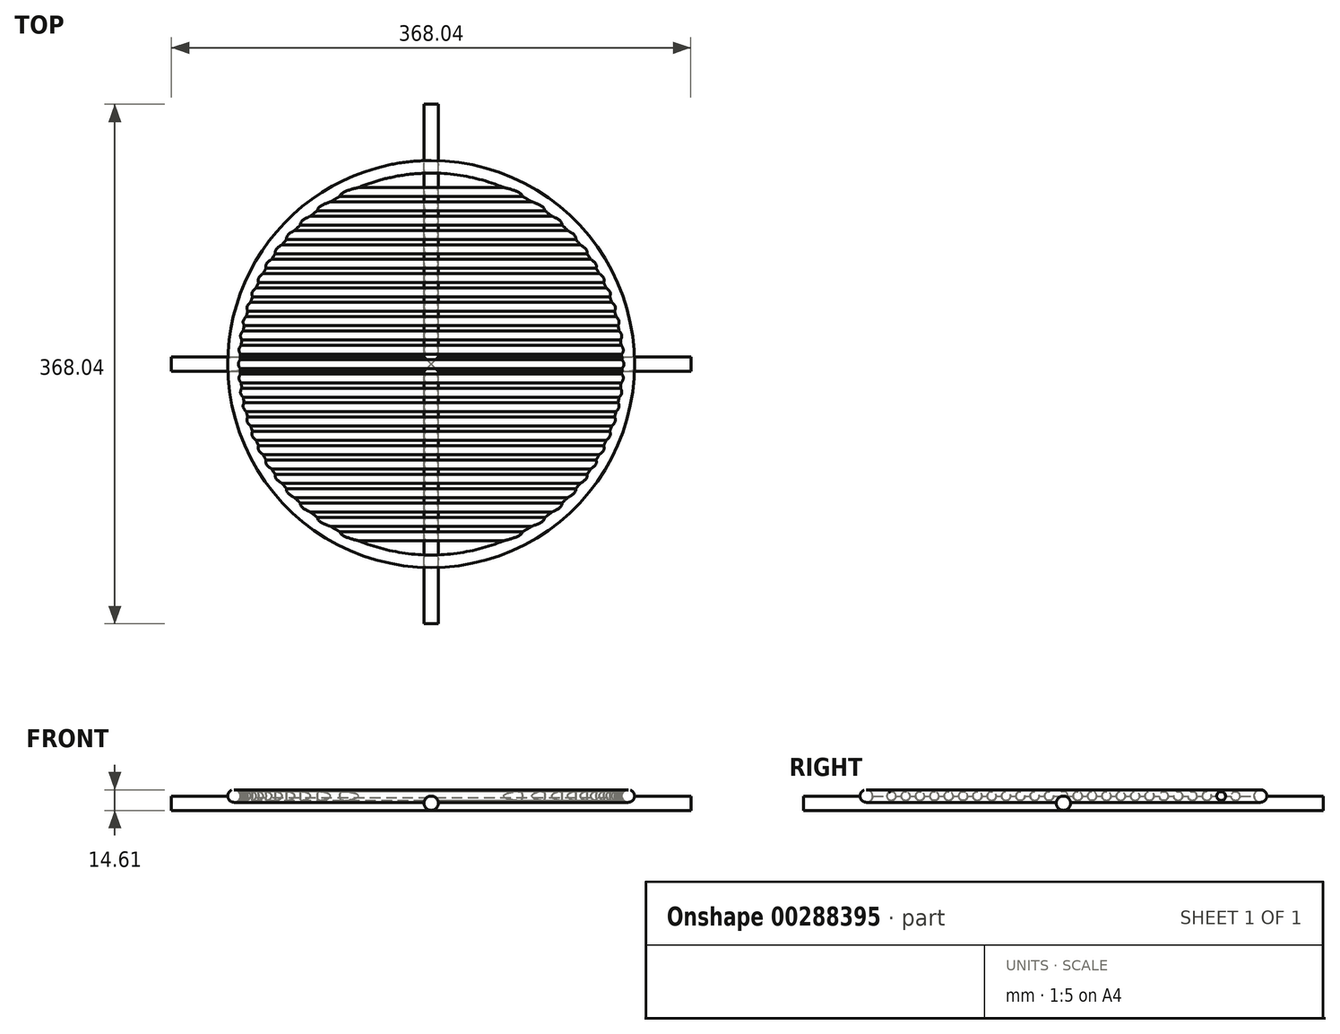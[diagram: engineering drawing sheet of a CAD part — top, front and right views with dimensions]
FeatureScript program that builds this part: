
annotation { "Feature Type Name" : "Feature", "Feature Type Description" : "" }
export const myFeature = defineFeature(function(context is Context, id is Id, definition is map)
    precondition{}
    {
        {
            var Q0;
            Q0=qCreatedBy(makeId("Top.planeOp"),FACE);
            var sketch = newSketch(context, id + "F0", { "sketchPlane" : qUnion([Q0])});
            skCircle(sketch, "E0.0.0", {"center": v(0, 0) * mm, "radius": 158.75 * mm, "construction": true});
            skCircle(sketch, "E1.0", {"center": v(0, 0) * mm, "radius": 139.7 * mm, "construction": true});
            skLineSegment(sketch, "E2", {"start": v(-158.62, 0) * mm, "end": v(158.62, 0) * mm});
            skLineSegment(sketch, "E3", {"start": v(0, 158.62) * mm, "end": v(0, -158.62) * mm});
            skLineSegment(sketch, "E4.bottom", {"start": v(-6.35, 158.62) * mm, "end": v(6.35, 158.62) * mm, "construction": true});
            skLineSegment(sketch, "E4.top", {"start": v(-6.35, 139.56) * mm, "end": v(6.35, 139.56) * mm, "construction": true});
            skLineSegment(sketch, "E4.left", {"start": v(-6.35, 158.62) * mm, "end": v(-6.35, 139.56) * mm, "construction": true});
            skLineSegment(sketch, "E4.right", {"start": v(6.35, 158.62) * mm, "end": v(6.35, 139.56) * mm, "construction": true});
            skLineSegment(sketch, "E5.bottom", {"start": v(-158.62, -6.35) * mm, "end": v(-139.56, -6.35) * mm, "construction": true});
            skLineSegment(sketch, "E5.top", {"start": v(-158.62, 6.35) * mm, "end": v(-139.56, 6.35) * mm, "construction": true});
            skLineSegment(sketch, "E5.left", {"start": v(-158.62, -6.35) * mm, "end": v(-158.62, 6.35) * mm, "construction": true});
            skLineSegment(sketch, "E5.right", {"start": v(-139.56, -6.35) * mm, "end": v(-139.56, 6.35) * mm, "construction": true});
            skLineSegment(sketch, "E6.bottom", {"start": v(158.62, 6.35) * mm, "end": v(139.56, 6.35) * mm, "construction": true});
            skLineSegment(sketch, "E6.top", {"start": v(158.62, -6.35) * mm, "end": v(139.56, -6.35) * mm, "construction": true});
            skLineSegment(sketch, "E6.left", {"start": v(158.62, 6.35) * mm, "end": v(158.62, -6.35) * mm, "construction": true});
            skLineSegment(sketch, "E6.right", {"start": v(139.56, 6.35) * mm, "end": v(139.56, -6.35) * mm, "construction": true});
            skLineSegment(sketch, "E7.bottom", {"start": v(6.35, -158.62) * mm, "end": v(-6.35, -158.62) * mm, "construction": true});
            skLineSegment(sketch, "E7.top", {"start": v(6.35, -139.56) * mm, "end": v(-6.35, -139.56) * mm, "construction": true});
            skLineSegment(sketch, "E7.left", {"start": v(6.35, -158.62) * mm, "end": v(6.35, -139.56) * mm, "construction": true});
            skLineSegment(sketch, "E7.right", {"start": v(-6.35, -158.62) * mm, "end": v(-6.35, -139.56) * mm, "construction": true});
            skPoint(sketch, "E8", {"position": v(158.62, 0) * mm});
            skPoint(sketch, "E9", {"position": v(0, -158.62) * mm});
            skPoint(sketch, "E10", {"position": v(0, 158.62) * mm});
            skPoint(sketch, "E11", {"position": v(-158.62, 0) * mm});
            skSolve(sketch);
        }
        {
            var Q0;
            Q0=sQuery(id+"F0.wireOp",VERTEX,"E11");
            var Q1;
            Q1=qCreatedBy(makeId("Right.planeOp"),FACE);
            cPlane(context, id + "F1", {"entities" : qUnion([Q0, Q1]), "cplaneType" : CPlaneType.PLANE_POINT, "offset" : 25.4 * mm, "width" : 152.4 * mm, "height" : 152.4 * mm});
        }
        {
            var Q0;
            Q0=qCreatedBy(id+"F1.planeOp",FACE);
            var sketch = newSketch(context, id + "F2", { "sketchPlane" : qUnion([Q0])});
            skPoint(sketch, "E12.0", {"position": v(0, 0) * mm});
            skCircle(sketch, "E13", {"center": v(0, 0) * mm, "radius": 5.08 * mm});
            skPoint(sketch, "E14", {"position": v(0, 5.08) * mm});
            skSolve(sketch);
        }
        {
            var Q0;
            Q0=sQuery(id+"F0.wireOp",VERTEX,"E9");
            var Q1;
            Q1=qCreatedBy(makeId("Front.planeOp"),FACE);
            cPlane(context, id + "F3", {"entities" : qUnion([Q0, Q1]), "cplaneType" : CPlaneType.PLANE_POINT, "offset" : 25.4 * mm, "width" : 152.4 * mm, "height" : 152.4 * mm});
        }
        {
            var Q0;
            Q0=qCreatedBy(id+"F3.planeOp",FACE);
            var sketch = newSketch(context, id + "F4", { "sketchPlane" : qUnion([Q0])});
            skCircle(sketch, "E15", {"center": v(0, 0) * mm, "radius": 5.08 * mm});
            skSolve(sketch);
        }
        {
            var Q0;
            Q0=sQuery(id+"F2.wireOp",VERTEX,"E14");
            var Q1;
            Q1=qCreatedBy(makeId("Top.planeOp"),FACE);
            cPlane(context, id + "F5", {"entities" : qUnion([Q0, Q1]), "cplaneType" : CPlaneType.PLANE_POINT, "offset" : 25.4 * mm, "width" : 152.4 * mm, "height" : 152.4 * mm});
        }
        {
            var Q0;
            Q0=qCreatedBy(id+"F5.planeOp",FACE);
            var sketch = newSketch(context, id + "F6", { "sketchPlane" : qUnion([Q0])});
            skCircle(sketch, "E16.0", {"center": v(0, 0) * mm, "radius": 139.7 * mm});
            skLineSegment(sketch, "E17", {"start": v(-139.7, 0) * mm, "end": v(139.7, 0) * mm});
            skLineSegment(sketch, "E18", {"start": v(-139.33, -10.16) * mm, "end": v(139.33, -10.16) * mm});
            skLineSegment(sketch, "E19", {"start": v(-138.21, -20.32) * mm, "end": v(138.21, -20.32) * mm});
            skLineSegment(sketch, "E20", {"start": v(136.33, -30.48) * mm, "end": v(-136.33, -30.48) * mm});
            skLineSegment(sketch, "E21", {"start": v(-133.66, -40.64) * mm, "end": v(133.66, -40.64) * mm});
            skLineSegment(sketch, "E22", {"start": v(130.14, -50.8) * mm, "end": v(-130.14, -50.8) * mm});
            skLineSegment(sketch, "E23", {"start": v(-125.7, -60.96) * mm, "end": v(125.7, -60.96) * mm});
            skLineSegment(sketch, "E24", {"start": v(120.24, -71.12) * mm, "end": v(-120.24, -71.12) * mm});
            skLineSegment(sketch, "E25", {"start": v(-113.62, -81.28) * mm, "end": v(113.62, -81.28) * mm});
            skLineSegment(sketch, "E26", {"start": v(-105.62, -91.44) * mm, "end": v(105.62, -91.44) * mm});
            skLineSegment(sketch, "E27", {"start": v(-95.88, -101.6) * mm, "end": v(95.88, -101.6) * mm});
            skLineSegment(sketch, "E28", {"start": v(-83.82, -111.76) * mm, "end": v(83.82, -111.76) * mm});
            skLineSegment(sketch, "E29", {"start": v(-68.2, -121.92) * mm, "end": v(68.2, -121.92) * mm});
            skLineSegment(sketch, "E30", {"start": v(0, 139.7) * mm, "end": v(0, -139.7) * mm, "construction": true});
            skLineSegment(sketch, "E31.MirrorCS", {"start": v(-139.33, 10.16) * mm, "end": v(139.33, 10.16) * mm});
            skLineSegment(sketch, "E32.MirrorCS", {"start": v(-138.21, 20.32) * mm, "end": v(138.21, 20.32) * mm});
            skLineSegment(sketch, "E33.MirrorCS", {"start": v(136.33, 30.48) * mm, "end": v(-136.33, 30.48) * mm});
            skLineSegment(sketch, "E34.MirrorCS", {"start": v(-133.66, 40.64) * mm, "end": v(133.66, 40.64) * mm});
            skLineSegment(sketch, "E35.MirrorCS", {"start": v(130.14, 50.8) * mm, "end": v(-130.14, 50.8) * mm});
            skLineSegment(sketch, "E36.MirrorCS", {"start": v(-125.7, 60.96) * mm, "end": v(125.7, 60.96) * mm});
            skLineSegment(sketch, "E37.MirrorCS", {"start": v(120.24, 71.12) * mm, "end": v(-120.24, 71.12) * mm});
            skLineSegment(sketch, "E38.MirrorCS", {"start": v(-113.62, 81.28) * mm, "end": v(113.62, 81.28) * mm});
            skLineSegment(sketch, "E39.MirrorCS", {"start": v(-105.62, 91.44) * mm, "end": v(105.62, 91.44) * mm});
            skLineSegment(sketch, "E40.MirrorCS", {"start": v(-95.88, 101.6) * mm, "end": v(95.88, 101.6) * mm});
            skLineSegment(sketch, "E41.MirrorCS", {"start": v(-83.82, 111.76) * mm, "end": v(83.82, 111.76) * mm});
            skLineSegment(sketch, "E42.MirrorCS", {"start": v(-68.2, 121.92) * mm, "end": v(68.2, 121.92) * mm});
            skSolve(sketch);
        }
        {
            var Q0;
            Q0=sQuery(id+"F6.wireOp",VERTEX,"E30.start");
            var Q1;
            Q1=qCreatedBy(makeId("Right.planeOp"),FACE);
            cPlane(context, id + "F7", {"entities" : qUnion([Q0, Q1]), "cplaneType" : CPlaneType.PLANE_POINT, "offset" : 25.4 * mm, "width" : 152.4 * mm, "height" : 152.4 * mm});
        }
        {
            var Q0;
            Q0=qCreatedBy(id+"F7.planeOp",FACE);
            var sketch = newSketch(context, id + "F8", { "sketchPlane" : qUnion([Q0])});
            skPoint(sketch, "E43.0", {"position": v(139.7, 5.08) * mm});
            skCircle(sketch, "E44", {"center": v(139.7, 5.08) * mm, "radius": 4.45 * mm});
            skSolve(sketch);
        }
        {
            var Q0;
            Q0=makeQuery(id+"F8.imprint","IMPRINT",FACE,{"disambiguationData":[TD([[makeQuery(id+"F8.imprint","IMPRINT",EDGE,{"derivedFrom":sQuery(id+"F8.wireOp",EDGE,"E44")}),1.0]])]});
            var Q1;
            Q1=sQuery(id+"F6.wireOp",EDGE,"E16.0");
            sweep(context, id + "F9", {"profiles" : qUnion([Q0]), "path" : qUnion([Q1])});
        }
        {
            var Q0;
            Q0=sQuery(id+"F6.wireOp",VERTEX,"E42.MirrorCS.end");
            var Q1;
            Q1=qCreatedBy(makeId("Right.planeOp"),FACE);
            cPlane(context, id + "F10", {"entities" : qUnion([Q0, Q1]), "cplaneType" : CPlaneType.PLANE_POINT, "offset" : 25.4 * mm, "width" : 152.4 * mm, "height" : 152.4 * mm});
        }
        {
            var Q0;
            Q0=qCreatedBy(id+"F10.planeOp",FACE);
            var sketch = newSketch(context, id + "F11", { "sketchPlane" : qUnion([Q0])});
            skPoint(sketch, "E45.0", {"position": v(121.92, 5.08) * mm});
            skCircle(sketch, "E46", {"center": v(121.92, 5.08) * mm, "radius": 3.18 * mm});
            skSolve(sketch);
        }
        {
            var Q0;
            Q0=sQuery(id+"F6.wireOp",VERTEX,"E41.MirrorCS.end");
            var Q1;
            Q1=qCreatedBy(id+"F10.planeOp",FACE);
            cPlane(context, id + "F12", {"entities" : qUnion([Q0, Q1]), "cplaneType" : CPlaneType.PLANE_POINT, "offset" : 25.4 * mm, "width" : 152.4 * mm, "height" : 152.4 * mm});
        }
        {
            var Q0;
            Q0=qCreatedBy(id+"F12.planeOp",FACE);
            var sketch = newSketch(context, id + "F13", { "sketchPlane" : qUnion([Q0])});
            skPoint(sketch, "E47.0", {"position": v(111.76, 5.08) * mm});
            skCircle(sketch, "E48", {"center": v(111.76, 5.08) * mm, "radius": 3.18 * mm});
            skSolve(sketch);
        }
        {
            var Q0;
            Q0=makeQuery(id+"F13.imprint","IMPRINT",FACE,{"disambiguationData":[TD([[makeQuery(id+"F13.imprint","IMPRINT",EDGE,{"derivedFrom":sQuery(id+"F13.wireOp",EDGE,"E48")}),1.0]])]});
            var Q1;
            Q1=sQuery(id+"F6.wireOp",EDGE,"E41.MirrorCS");
            sweep(context, id + "F14", {"profiles" : qUnion([Q0]), "path" : qUnion([Q1])});
        }
        {
            var Q0;
            Q0=makeQuery(id+"F11.imprint","IMPRINT",FACE,{"disambiguationData":[TD([[makeQuery(id+"F11.imprint","IMPRINT",EDGE,{"derivedFrom":sQuery(id+"F11.wireOp",EDGE,"E46")}),1.0]])]});
            var Q1;
            Q1=sQuery(id+"F6.wireOp",EDGE,"E42.MirrorCS");
            sweep(context, id + "F15", {"profiles" : qUnion([Q0]), "path" : qUnion([Q1])});
        }
        {
            var Q0;
            Q0=sQuery(id+"F6.wireOp",VERTEX,"E40.MirrorCS.end");
            var Q1;
            Q1=qCreatedBy(id+"F12.planeOp",FACE);
            cPlane(context, id + "F16", {"entities" : qUnion([Q0, Q1]), "cplaneType" : CPlaneType.PLANE_POINT, "offset" : 25.4 * mm, "width" : 152.4 * mm, "height" : 152.4 * mm});
        }
        {
            var Q0;
            Q0=qCreatedBy(id+"F16.planeOp",FACE);
            var sketch = newSketch(context, id + "F17", { "sketchPlane" : qUnion([Q0])});
            skPoint(sketch, "E49.0", {"position": v(101.6, 5.08) * mm});
            skCircle(sketch, "E50", {"center": v(101.6, 5.08) * mm, "radius": 3.18 * mm});
            skSolve(sketch);
        }
        {
            var Q0;
            Q0=makeQuery(id+"F17.imprint","IMPRINT",FACE,{"disambiguationData":[TD([[makeQuery(id+"F17.imprint","IMPRINT",EDGE,{"derivedFrom":sQuery(id+"F17.wireOp",EDGE,"E50")}),1.0]])]});
            var Q1;
            Q1=sQuery(id+"F6.wireOp",EDGE,"E40.MirrorCS");
            sweep(context, id + "F18", {"operationType" : NewBodyOperationType.ADD, "profiles" : qUnion([Q0]), "path" : qUnion([Q1])});
        }
        {
            var Q0;
            Q0=makeQuery(id+"F17.imprint","IMPRINT",FACE,{"disambiguationData":[TD([[makeQuery(id+"F17.imprint","IMPRINT",EDGE,{"derivedFrom":sQuery(id+"F17.wireOp",EDGE,"E50")}),1.0]])]});
            var Q1;
            Q1=sQuery(id+"F6.wireOp",EDGE,"E40.MirrorCS");
            sweep(context, id + "F19", {"profiles" : qUnion([Q0]), "path" : qUnion([Q1])});
        }
        {
            var Q0;
            Q0=sQuery(id+"F6.wireOp",VERTEX,"E39.MirrorCS.end");
            var Q1;
            Q1=qCreatedBy(id+"F16.planeOp",FACE);
            cPlane(context, id + "F20", {"entities" : qUnion([Q0, Q1]), "cplaneType" : CPlaneType.PLANE_POINT, "offset" : 25.4 * mm, "width" : 152.4 * mm, "height" : 152.4 * mm});
        }
        {
            var Q0;
            Q0=qCreatedBy(id+"F20.planeOp",FACE);
            var sketch = newSketch(context, id + "F21", { "sketchPlane" : qUnion([Q0])});
            skPoint(sketch, "E51.0", {"position": v(91.44, 5.08) * mm});
            skCircle(sketch, "E52", {"center": v(91.44, 5.08) * mm, "radius": 3.18 * mm});
            skSolve(sketch);
        }
        {
            var Q0;
            Q0=makeQuery(id+"F21.imprint","IMPRINT",FACE,{"disambiguationData":[TD([[makeQuery(id+"F21.imprint","IMPRINT",EDGE,{"derivedFrom":sQuery(id+"F21.wireOp",EDGE,"E52")}),1.0]])]});
            var Q1;
            Q1=sQuery(id+"F6.wireOp",EDGE,"E39.MirrorCS");
            sweep(context, id + "F22", {"profiles" : qUnion([Q0]), "path" : qUnion([Q1])});
        }
        {
            var Q0;
            Q0=sQuery(id+"F6.wireOp",VERTEX,"E38.MirrorCS.end");
            var Q1;
            Q1=qCreatedBy(id+"F16.planeOp",FACE);
            cPlane(context, id + "F23", {"entities" : qUnion([Q0, Q1]), "cplaneType" : CPlaneType.PLANE_POINT, "offset" : 25.4 * mm, "width" : 152.4 * mm, "height" : 152.4 * mm});
        }
        {
            var Q0;
            Q0=qCreatedBy(id+"F23.planeOp",FACE);
            var sketch = newSketch(context, id + "F24", { "sketchPlane" : qUnion([Q0])});
            skPoint(sketch, "E53.0", {"position": v(81.28, 5.08) * mm});
            skCircle(sketch, "E54", {"center": v(81.28, 5.08) * mm, "radius": 3.18 * mm});
            skSolve(sketch);
        }
        {
            var Q0;
            Q0=sQuery(id+"F6.wireOp",VERTEX,"E37.MirrorCS.start");
            var Q1;
            Q1=qCreatedBy(id+"F16.planeOp",FACE);
            cPlane(context, id + "F25", {"entities" : qUnion([Q0, Q1]), "cplaneType" : CPlaneType.PLANE_POINT, "offset" : 25.4 * mm, "width" : 152.4 * mm, "height" : 152.4 * mm});
        }
        {
            var Q0;
            Q0=qCreatedBy(id+"F25.planeOp",FACE);
            var sketch = newSketch(context, id + "F26", { "sketchPlane" : qUnion([Q0])});
            skPoint(sketch, "E55.0", {"position": v(71.12, 5.08) * mm});
            skCircle(sketch, "E56", {"center": v(71.12, 5.08) * mm, "radius": 3.18 * mm});
            skSolve(sketch);
        }
        {
            var Q0;
            Q0=sQuery(id+"F6.wireOp",VERTEX,"E36.MirrorCS.end");
            var Q1;
            Q1=qCreatedBy(id+"F16.planeOp",FACE);
            cPlane(context, id + "F27", {"entities" : qUnion([Q0, Q1]), "cplaneType" : CPlaneType.PLANE_POINT, "offset" : 25.4 * mm, "width" : 152.4 * mm, "height" : 152.4 * mm});
        }
        {
            var Q0;
            Q0=qCreatedBy(id+"F27.planeOp",FACE);
            var sketch = newSketch(context, id + "F28", { "sketchPlane" : qUnion([Q0])});
            skPoint(sketch, "E57.0", {"position": v(60.96, 5.08) * mm});
            skCircle(sketch, "E58", {"center": v(60.96, 5.08) * mm, "radius": 3.18 * mm});
            skSolve(sketch);
        }
        {
            var Q0;
            Q0=sQuery(id+"F6.wireOp",VERTEX,"E35.MirrorCS.start");
            var Q1;
            Q1=qCreatedBy(id+"F16.planeOp",FACE);
            cPlane(context, id + "F29", {"entities" : qUnion([Q0, Q1]), "cplaneType" : CPlaneType.PLANE_POINT, "offset" : 25.4 * mm, "width" : 152.4 * mm, "height" : 152.4 * mm});
        }
        {
            var Q0;
            Q0=qCreatedBy(id+"F29.planeOp",FACE);
            var sketch = newSketch(context, id + "F30", { "sketchPlane" : qUnion([Q0])});
            skPoint(sketch, "E59.0", {"position": v(50.8, 5.08) * mm});
            skCircle(sketch, "E60", {"center": v(50.8, 5.08) * mm, "radius": 3.18 * mm});
            skSolve(sketch);
        }
        {
            var Q0;
            Q0=sQuery(id+"F6.wireOp",VERTEX,"E34.MirrorCS.end");
            var Q1;
            Q1=qCreatedBy(id+"F16.planeOp",FACE);
            cPlane(context, id + "F31", {"entities" : qUnion([Q0, Q1]), "cplaneType" : CPlaneType.PLANE_POINT, "offset" : 25.4 * mm, "width" : 152.4 * mm, "height" : 152.4 * mm});
        }
        {
            var Q0;
            Q0=qCreatedBy(id+"F31.planeOp",FACE);
            var sketch = newSketch(context, id + "F32", { "sketchPlane" : qUnion([Q0])});
            skPoint(sketch, "E61.0", {"position": v(40.64, 5.08) * mm});
            skCircle(sketch, "E62", {"center": v(40.64, 5.08) * mm, "radius": 3.18 * mm});
            skSolve(sketch);
        }
        {
            var Q0;
            Q0=sQuery(id+"F6.wireOp",VERTEX,"E33.MirrorCS.start");
            var Q1;
            Q1=qCreatedBy(id+"F10.planeOp",FACE);
            cPlane(context, id + "F33", {"entities" : qUnion([Q0, Q1]), "cplaneType" : CPlaneType.PLANE_POINT, "offset" : 25.4 * mm, "width" : 152.4 * mm, "height" : 152.4 * mm});
        }
        {
            var Q0;
            Q0=qCreatedBy(id+"F33.planeOp",FACE);
            var sketch = newSketch(context, id + "F34", { "sketchPlane" : qUnion([Q0])});
            skPoint(sketch, "E63.0", {"position": v(30.48, 5.08) * mm});
            skCircle(sketch, "E64", {"center": v(30.48, 5.08) * mm, "radius": 3.17 * mm});
            skSolve(sketch);
        }
        {
            var Q0;
            Q0=sQuery(id+"F6.wireOp",VERTEX,"E32.MirrorCS.end");
            var Q1;
            Q1=qCreatedBy(id+"F12.planeOp",FACE);
            cPlane(context, id + "F35", {"entities" : qUnion([Q0, Q1]), "cplaneType" : CPlaneType.PLANE_POINT, "offset" : 25.4 * mm, "width" : 152.4 * mm, "height" : 152.4 * mm});
        }
        {
            var Q0;
            Q0=qCreatedBy(id+"F35.planeOp",FACE);
            var sketch = newSketch(context, id + "F36", { "sketchPlane" : qUnion([Q0])});
            skPoint(sketch, "E65.0", {"position": v(20.32, 5.08) * mm});
            skCircle(sketch, "E66", {"center": v(20.32, 5.08) * mm, "radius": 3.18 * mm});
            skSolve(sketch);
        }
        {
            var Q0;
            Q0=sQuery(id+"F6.wireOp",VERTEX,"E31.MirrorCS.end");
            var Q1;
            Q1=qCreatedBy(id+"F31.planeOp",FACE);
            cPlane(context, id + "F37", {"entities" : qUnion([Q0, Q1]), "cplaneType" : CPlaneType.PLANE_POINT, "offset" : 25.4 * mm, "width" : 152.4 * mm, "height" : 152.4 * mm});
        }
        {
            var Q0;
            Q0=qCreatedBy(id+"F37.planeOp",FACE);
            var sketch = newSketch(context, id + "F38", { "sketchPlane" : qUnion([Q0])});
            skPoint(sketch, "E67.0", {"position": v(10.16, 5.08) * mm});
            skCircle(sketch, "E68", {"center": v(10.16, 5.08) * mm, "radius": 3.18 * mm});
            skSolve(sketch);
        }
        {
            var Q0;
            Q0=sQuery(id+"F6.wireOp",VERTEX,"E17.end");
            var Q1;
            Q1=qCreatedBy(id+"F16.planeOp",FACE);
            cPlane(context, id + "F39", {"entities" : qUnion([Q0, Q1]), "cplaneType" : CPlaneType.PLANE_POINT, "offset" : 25.4 * mm, "width" : 152.4 * mm, "height" : 152.4 * mm});
        }
        {
            var Q0;
            Q0=qCreatedBy(id+"F39.planeOp",FACE);
            var sketch = newSketch(context, id + "F40", { "sketchPlane" : qUnion([Q0])});
            skPoint(sketch, "E69.0", {"position": v(0, 5.08) * mm});
            skCircle(sketch, "E70", {"center": v(0, 5.08) * mm, "radius": 3.18 * mm});
            skSolve(sketch);
        }
        {
            var Q0;
            Q0=makeQuery(id+"F24.imprint","IMPRINT",FACE,{"disambiguationData":[TD([[makeQuery(id+"F24.imprint","IMPRINT",EDGE,{"derivedFrom":sQuery(id+"F24.wireOp",EDGE,"E54")}),1.0]])]});
            var Q1;
            Q1=sQuery(id+"F6.wireOp",EDGE,"E38.MirrorCS");
            sweep(context, id + "F41", {"profiles" : qUnion([Q0]), "path" : qUnion([Q1])});
        }
        {
            var Q0;
            Q0=makeQuery(id+"F26.imprint","IMPRINT",FACE,{"disambiguationData":[TD([[makeQuery(id+"F26.imprint","IMPRINT",EDGE,{"derivedFrom":sQuery(id+"F26.wireOp",EDGE,"E56")}),1.0]])]});
            var Q1;
            Q1=sQuery(id+"F6.wireOp",EDGE,"E37.MirrorCS");
            sweep(context, id + "F42", {"profiles" : qUnion([Q0]), "path" : qUnion([Q1])});
        }
        {
            var Q0;
            Q0=makeQuery(id+"F28.imprint","IMPRINT",FACE,{"disambiguationData":[TD([[makeQuery(id+"F28.imprint","IMPRINT",EDGE,{"derivedFrom":sQuery(id+"F28.wireOp",EDGE,"E58")}),1.0]])]});
            var Q1;
            Q1=sQuery(id+"F6.wireOp",EDGE,"E36.MirrorCS");
            sweep(context, id + "F43", {"profiles" : qUnion([Q0]), "path" : qUnion([Q1])});
        }
        {
            var Q0;
            Q0=makeQuery(id+"F30.imprint","IMPRINT",FACE,{"disambiguationData":[TD([[makeQuery(id+"F30.imprint","IMPRINT",EDGE,{"derivedFrom":sQuery(id+"F30.wireOp",EDGE,"E60")}),1.0]])]});
            var Q1;
            Q1=sQuery(id+"F6.wireOp",EDGE,"E35.MirrorCS");
            sweep(context, id + "F44", {"profiles" : qUnion([Q0]), "path" : qUnion([Q1])});
        }
        {
            var Q0;
            Q0=makeQuery(id+"F32.imprint","IMPRINT",FACE,{"disambiguationData":[TD([[makeQuery(id+"F32.imprint","IMPRINT",EDGE,{"derivedFrom":sQuery(id+"F32.wireOp",EDGE,"E62")}),1.0]])]});
            var Q1;
            Q1=sQuery(id+"F6.wireOp",EDGE,"E34.MirrorCS");
            sweep(context, id + "F45", {"profiles" : qUnion([Q0]), "path" : qUnion([Q1])});
        }
        {
            var Q0;
            Q0=makeQuery(id+"F34.imprint","IMPRINT",FACE,{"disambiguationData":[TD([[makeQuery(id+"F34.imprint","IMPRINT",EDGE,{"derivedFrom":sQuery(id+"F34.wireOp",EDGE,"E64")}),1.0]])]});
            var Q1;
            Q1=sQuery(id+"F6.wireOp",EDGE,"E33.MirrorCS");
            sweep(context, id + "F46", {"profiles" : qUnion([Q0]), "path" : qUnion([Q1])});
        }
        {
            var Q0;
            Q0=makeQuery(id+"F36.imprint","IMPRINT",FACE,{"disambiguationData":[TD([[makeQuery(id+"F36.imprint","IMPRINT",EDGE,{"derivedFrom":sQuery(id+"F36.wireOp",EDGE,"E66")}),1.0]])]});
            var Q1;
            Q1=sQuery(id+"F6.wireOp",EDGE,"E32.MirrorCS");
            sweep(context, id + "F47", {"profiles" : qUnion([Q0]), "path" : qUnion([Q1])});
        }
        {
            var Q0;
            Q0=makeQuery(id+"F38.imprint","IMPRINT",FACE,{"disambiguationData":[TD([[makeQuery(id+"F38.imprint","IMPRINT",EDGE,{"derivedFrom":sQuery(id+"F38.wireOp",EDGE,"E68")}),1.0]])]});
            var Q1;
            Q1=sQuery(id+"F6.wireOp",EDGE,"E31.MirrorCS");
            sweep(context, id + "F48", {"profiles" : qUnion([Q0]), "path" : qUnion([Q1])});
        }
        {
            var Q0;
            Q0=makeQuery(id+"F40.imprint","IMPRINT",FACE,{"disambiguationData":[TD([[makeQuery(id+"F40.imprint","IMPRINT",EDGE,{"derivedFrom":sQuery(id+"F40.wireOp",EDGE,"E70")}),1.0]])]});
            var Q1;
            Q1=sQuery(id+"F6.wireOp",EDGE,"E17");
            sweep(context, id + "F49", {"profiles" : qUnion([Q0]), "path" : qUnion([Q1])});
        }
        {
            var Q0;
            Q0=makeQuery(id+"F14.opSweep","SWEPT_BODY",BODY,{"disambiguationData":[OSD([sQuery(id+"F6.wireOp",EDGE,"E41.MirrorCS"),sQuery(id+"F13.wireOp",EDGE,"E48")])]});
            var Q1;
            Q1=makeQuery(id+"F15.opSweep","SWEPT_BODY",BODY,{"disambiguationData":[OSD([sQuery(id+"F6.wireOp",EDGE,"E42.MirrorCS"),sQuery(id+"F11.wireOp",EDGE,"E46")])]});
            var Q2;
            Q2=makeQuery(id+"F19.opSweep","SWEPT_BODY",BODY,{"disambiguationData":[OSD([sQuery(id+"F6.wireOp",EDGE,"E40.MirrorCS"),sQuery(id+"F17.wireOp",EDGE,"E50")])]});
            var Q3;
            Q3=makeQuery(id+"F22.opSweep","SWEPT_BODY",BODY,{"disambiguationData":[OSD([sQuery(id+"F6.wireOp",EDGE,"E39.MirrorCS"),sQuery(id+"F21.wireOp",EDGE,"E52")])]});
            var Q4;
            Q4=makeQuery(id+"F41.opSweep","SWEPT_BODY",BODY,{"disambiguationData":[OSD([sQuery(id+"F6.wireOp",EDGE,"E38.MirrorCS"),sQuery(id+"F24.wireOp",EDGE,"E54")])]});
            var Q5;
            Q5=makeQuery(id+"F42.opSweep","SWEPT_BODY",BODY,{"disambiguationData":[OSD([sQuery(id+"F6.wireOp",EDGE,"E37.MirrorCS"),sQuery(id+"F26.wireOp",EDGE,"E56")])]});
            var Q6;
            Q6=makeQuery(id+"F43.opSweep","SWEPT_BODY",BODY,{"disambiguationData":[OSD([sQuery(id+"F6.wireOp",EDGE,"E36.MirrorCS"),sQuery(id+"F28.wireOp",EDGE,"E58")])]});
            var Q7;
            Q7=makeQuery(id+"F44.opSweep","SWEPT_BODY",BODY,{"disambiguationData":[OSD([sQuery(id+"F6.wireOp",EDGE,"E35.MirrorCS"),sQuery(id+"F30.wireOp",EDGE,"E60")])]});
            var Q8;
            Q8=makeQuery(id+"F45.opSweep","SWEPT_BODY",BODY,{"disambiguationData":[OSD([sQuery(id+"F6.wireOp",EDGE,"E34.MirrorCS"),sQuery(id+"F32.wireOp",EDGE,"E62")])]});
            var Q9;
            Q9=makeQuery(id+"F46.opSweep","SWEPT_BODY",BODY,{"disambiguationData":[OSD([sQuery(id+"F6.wireOp",EDGE,"E33.MirrorCS"),sQuery(id+"F34.wireOp",EDGE,"E64")])]});
            var Q10;
            Q10=makeQuery(id+"F47.opSweep","SWEPT_BODY",BODY,{"disambiguationData":[OSD([sQuery(id+"F6.wireOp",EDGE,"E32.MirrorCS"),sQuery(id+"F36.wireOp",EDGE,"E66")])]});
            var Q11;
            Q11=makeQuery(id+"F48.opSweep","SWEPT_BODY",BODY,{"disambiguationData":[OSD([sQuery(id+"F6.wireOp",EDGE,"E31.MirrorCS"),sQuery(id+"F38.wireOp",EDGE,"E68")])]});
            var Q12;
            Q12=makeQuery(id+"F49.opSweep","SWEPT_BODY",BODY,{"disambiguationData":[OSD([sQuery(id+"F6.wireOp",EDGE,"E17"),sQuery(id+"F40.wireOp",EDGE,"E70")])]});
            var Q13;
            Q13=qCreatedBy(makeId("Front.planeOp"),FACE);
            mirror(context, id + "F50", {"operationType" : NewBodyOperationType.ADD, "entities" : qUnion([Q0, Q1, Q2, Q3, Q4, Q5, Q6, Q7, Q8, Q9, Q10, Q11, Q12]), "mirrorPlane" : qUnion([Q13])});
        }
        {
            var Q0;
            Q0=makeQuery(id+"F2.imprint","IMPRINT",FACE,{"disambiguationData":[TD([[makeQuery(id+"F2.imprint","IMPRINT",EDGE,{"derivedFrom":sQuery(id+"F2.wireOp",EDGE,"E13")}),1.0]])]});
            var Q1;
            Q1=sQuery(id+"F0.wireOp",EDGE,"E2");
            sweep(context, id + "F51", {"operationType" : NewBodyOperationType.ADD, "profiles" : qUnion([Q0]), "path" : qUnion([Q1])});
        }
        {
            var Q0;
            Q0=makeQuery(id+"F4.imprint","IMPRINT",FACE,{"disambiguationData":[TD([[makeQuery(id+"F4.imprint","IMPRINT",EDGE,{"derivedFrom":sQuery(id+"F4.wireOp",EDGE,"E15")}),1.0]])]});
            var Q1;
            Q1=sQuery(id+"F0.wireOp",EDGE,"E3");
            sweep(context, id + "F52", {"operationType" : NewBodyOperationType.ADD, "profiles" : qUnion([Q0]), "path" : qUnion([Q1])});
        }
        {
            var Q0;
            Q0=makeQuery(id+"F52.opSweep","CAP_FACE",FACE,{"disambiguationData":[OSD([sQuery(id+"F0.wireOp",VERTEX,"E3.end"),sQuery(id+"F4.wireOp",EDGE,"E15")])],"isStart":true});
            extrude(context, id + "F53", {"entities" : qUnion([Q0]), "operationType" : NewBodyOperationType.ADD, "depth" : 25.4 * mm});
        }
        {
            var Q0;
            Q0=makeQuery(id+"F51.opSweep","CAP_FACE",FACE,{"disambiguationData":[OSD([sQuery(id+"F0.wireOp",VERTEX,"E2.end"),sQuery(id+"F2.wireOp",EDGE,"E13")])],"isStart":false});
            extrude(context, id + "F54", {"entities" : qUnion([Q0]), "operationType" : NewBodyOperationType.ADD, "depth" : 25.4 * mm});
        }
        {
            var Q0;
            Q0=makeQuery(id+"F52.opSweep","CAP_FACE",FACE,{"disambiguationData":[OSD([sQuery(id+"F0.wireOp",VERTEX,"E3.start"),sQuery(id+"F4.wireOp",EDGE,"E15")])],"isStart":false});
            extrude(context, id + "F55", {"entities" : qUnion([Q0]), "operationType" : NewBodyOperationType.ADD, "depth" : 25.4 * mm});
        }
        {
            var Q0;
            Q0=makeQuery(id+"F51.opSweep","CAP_FACE",FACE,{"disambiguationData":[OSD([sQuery(id+"F0.wireOp",VERTEX,"E2.start"),sQuery(id+"F2.wireOp",EDGE,"E13")])],"isStart":true});
            extrude(context, id + "F56", {"entities" : qUnion([Q0]), "operationType" : NewBodyOperationType.ADD, "depth" : 25.4 * mm});
        }
    });
